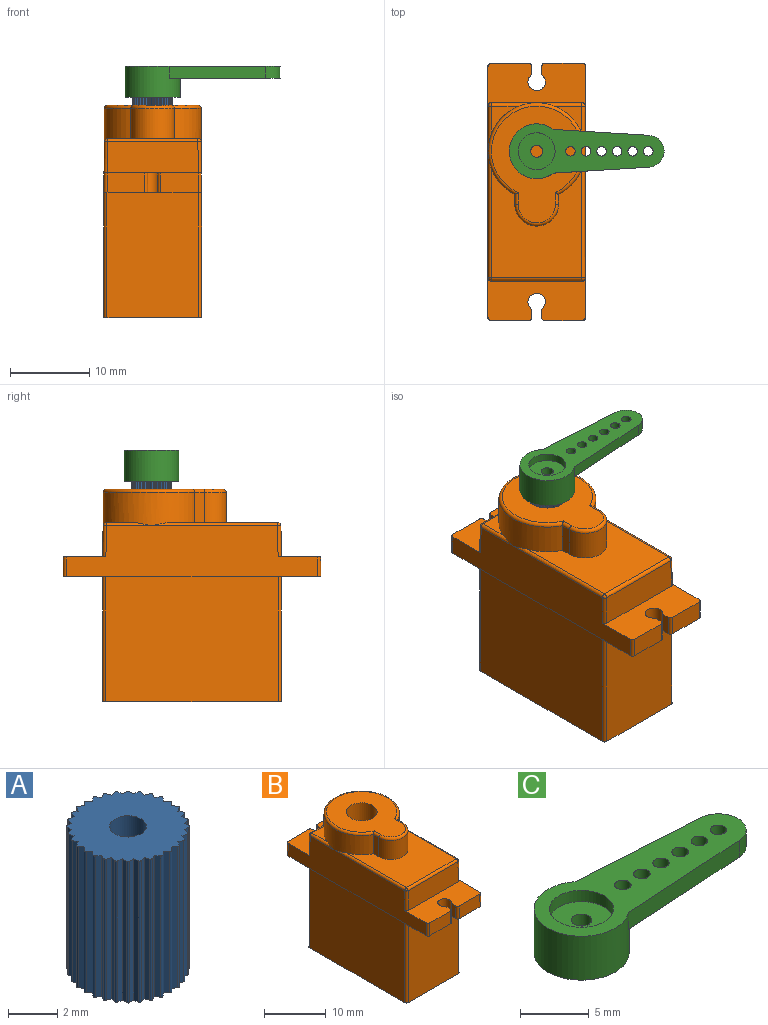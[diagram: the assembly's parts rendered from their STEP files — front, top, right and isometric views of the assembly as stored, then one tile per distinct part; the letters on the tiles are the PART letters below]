
ASSEMBLY  parts=3 mates=2
PART A: 99 faces, bbox 5x5x7.1 mm
  f0: plane 5x5mm, normal (0,0,-1), area 16.5mm2, adj f1,f2,f3,f4,f5,f6,f7,f8
  f1: plane 7.05x0.2mm, normal (-0.8,0.6,0), area 1.7mm2, adj f0,f2,f94,f95
  f2: cylinder r=0.08mm len=7.05mm, axis (0,0,-1), area 0.9mm2, adj f0,f1,f3,f94
  f3: plane 7.05x0.21mm, normal (-0.51,-0.86,0), area 1.7mm2, adj f0,f2,f4,f94
  f4: plane 7.05x0.22mm, normal (-0.9,0.43,0), area 1.7mm2, adj f0,f3,f5,f94
  f5: cylinder r=0.08mm len=7.05mm, axis (0,0,-1), area 0.9mm2, adj f0,f4,f6,f94
  f6: plane 7.05x0.23mm, normal (-0.33,-0.94,0), area 1.7mm2, adj f0,f5,f7,f94
  f7: plane 7.05x0.24mm, normal (-0.97,0.25,0), area 1.7mm2, adj f0,f6,f8,f94
  f8: cylinder r=0.08mm len=7.05mm, axis (0,0,-1), area 0.9mm2, adj f0,f7,f9,f94
  f9: plane 7.05x0.25mm, normal (-0.14,-0.99,0), area 1.7mm2, adj f0,f8,f10,f94
  f10: plane 7.05x0.25mm, normal (-1,0.05,0), area 1.7mm2, adj f0,f9,f11,f94
  f11: cylinder r=0.08mm len=7.05mm, axis (0,0,-1), area 0.9mm2, adj f0,f10,f12,f94
  f12: plane 7.05x0.25mm, normal (0.05,-1,0), area 1.7mm2, adj f0,f11,f13,f94
  f13: plane 7.05x0.25mm, normal (-0.99,-0.14,0), area 1.7mm2, adj f0,f12,f14,f94
  f14: cylinder r=0.08mm len=7.05mm, axis (0,0,-1), area 0.9mm2, adj f0,f13,f15,f94
  f15: plane 7.05x0.24mm, normal (0.25,-0.97,0), area 1.7mm2, adj f0,f14,f16,f94
  f16: plane 7.05x0.23mm, normal (-0.94,-0.33,0), area 1.7mm2, adj f0,f15,f17,f94
  f17: cylinder r=0.08mm len=7.05mm, axis (0,0,-1), area 0.9mm2, adj f0,f16,f18,f94
  f18: plane 7.05x0.22mm, normal (0.43,-0.9,0), area 1.7mm2, adj f0,f17,f19,f94
  f19: plane 7.05x0.21mm, normal (-0.86,-0.51,0), area 1.7mm2, adj f0,f18,f20,f94
  f20: cylinder r=0.08mm len=7.05mm, axis (0,0,-1), area 0.9mm2, adj f0,f19,f21,f94
  f21: plane 7.05x0.2mm, normal (0.6,-0.8,0), area 1.7mm2, adj f0,f20,f22,f94
  f22: plane 7.05x0.18mm, normal (-0.74,-0.67,0), area 1.7mm2, adj f0,f21,f23,f94
  f23: cylinder r=0.08mm len=7.05mm, axis (0,0,-1), area 0.9mm2, adj f0,f22,f24,f94
  f24: plane 7.05x0.18mm, normal (0.74,-0.67,0), area 1.7mm2, adj f0,f23,f25,f94
  f25: plane 7.05x0.2mm, normal (-0.6,-0.8,0), area 1.7mm2, adj f0,f24,f26,f94
  f26: cylinder r=0.08mm len=7.05mm, axis (0,0,-1), area 0.9mm2, adj f0,f25,f27,f94
  f27: plane 7.05x0.21mm, normal (0.86,-0.51,0), area 1.7mm2, adj f0,f26,f28,f94
  f28: plane 7.05x0.22mm, normal (-0.43,-0.9,0), area 1.7mm2, adj f0,f27,f29,f94
  f29: cylinder r=0.08mm len=7.05mm, axis (0,0,-1), area 0.9mm2, adj f0,f28,f30,f94
  f30: plane 7.05x0.23mm, normal (0.94,-0.33,0), area 1.7mm2, adj f0,f29,f31,f94
  f31: plane 7.05x0.24mm, normal (-0.25,-0.97,0), area 1.7mm2, adj f0,f30,f32,f94
  f32: cylinder r=0.08mm len=7.05mm, axis (0,0,-1), area 0.9mm2, adj f0,f31,f33,f94
  f33: plane 7.05x0.25mm, normal (0.99,-0.14,0), area 1.7mm2, adj f0,f32,f34,f94
  f34: plane 7.05x0.25mm, normal (-0.05,-1,0), area 1.7mm2, adj f0,f33,f35,f94
  f35: cylinder r=0.08mm len=7.05mm, axis (0,0,-1), area 0.9mm2, adj f0,f34,f36,f94
  f36: plane 7.05x0.25mm, normal (1,0.05,0), area 1.7mm2, adj f0,f35,f37,f94
  f37: plane 7.05x0.25mm, normal (0.14,-0.99,0), area 1.7mm2, adj f0,f36,f38,f94
  f38: cylinder r=0.08mm len=7.05mm, axis (0,0,-1), area 0.9mm2, adj f0,f37,f39,f94
  f39: plane 7.05x0.24mm, normal (0.97,0.25,0), area 1.7mm2, adj f0,f38,f40,f94
  f40: plane 7.05x0.23mm, normal (0.33,-0.94,0), area 1.7mm2, adj f0,f39,f41,f94
  f41: cylinder r=0.08mm len=7.05mm, axis (0,0,-1), area 0.9mm2, adj f0,f40,f42,f94
  f42: plane 7.05x0.22mm, normal (0.9,0.43,0), area 1.7mm2, adj f0,f41,f43,f94
  f43: plane 7.05x0.21mm, normal (0.51,-0.86,0), area 1.7mm2, adj f0,f42,f44,f94
  f44: cylinder r=0.08mm len=7.05mm, axis (0,0,-1), area 0.9mm2, adj f0,f43,f45,f94
  f45: plane 7.05x0.2mm, normal (0.8,0.6,0), area 1.7mm2, adj f0,f44,f46,f94
  f46: plane 7.05x0.18mm, normal (0.67,-0.74,0), area 1.7mm2, adj f0,f45,f47,f94
  f47: cylinder r=0.08mm len=7.05mm, axis (0,0,-1), area 0.9mm2, adj f0,f46,f48,f94
  f48: plane 7.05x0.18mm, normal (0.67,0.74,0), area 1.7mm2, adj f0,f47,f49,f94
  f49: plane 7.05x0.2mm, normal (0.8,-0.6,0), area 1.7mm2, adj f0,f48,f50,f94
  f50: cylinder r=0.08mm len=7.05mm, axis (0,0,-1), area 0.9mm2, adj f0,f49,f51,f94
  f51: plane 7.05x0.21mm, normal (0.51,0.86,0), area 1.7mm2, adj f0,f50,f52,f94
  f52: plane 7.05x0.22mm, normal (0.9,-0.43,0), area 1.7mm2, adj f0,f51,f53,f94
  f53: cylinder r=0.08mm len=7.05mm, axis (0,0,-1), area 0.9mm2, adj f0,f52,f54,f94
  f54: plane 7.05x0.23mm, normal (0.33,0.94,0), area 1.7mm2, adj f0,f53,f55,f94
  f55: plane 7.05x0.24mm, normal (0.97,-0.25,0), area 1.7mm2, adj f0,f54,f56,f94
  f56: cylinder r=0.08mm len=7.05mm, axis (0,0,-1), area 0.9mm2, adj f0,f55,f57,f94
  f57: plane 7.05x0.25mm, normal (0.14,0.99,0), area 1.7mm2, adj f0,f56,f58,f94
  f58: plane 7.05x0.25mm, normal (1,-0.05,0), area 1.7mm2, adj f0,f57,f59,f94
  f59: cylinder r=0.08mm len=7.05mm, axis (0,0,-1), area 0.9mm2, adj f0,f58,f60,f94
  f60: plane 7.05x0.25mm, normal (-0.05,1,0), area 1.7mm2, adj f0,f59,f61,f94
  f61: plane 7.05x0.25mm, normal (0.99,0.14,0), area 1.7mm2, adj f0,f60,f62,f94
  f62: cylinder r=0.08mm len=7.05mm, axis (0,0,-1), area 0.9mm2, adj f0,f61,f63,f94
  f63: plane 7.05x0.24mm, normal (-0.25,0.97,0), area 1.7mm2, adj f0,f62,f64,f94
  f64: plane 7.05x0.23mm, normal (0.94,0.33,0), area 1.7mm2, adj f0,f63,f65,f94
  f65: cylinder r=0.08mm len=7.05mm, axis (0,0,-1), area 0.9mm2, adj f0,f64,f66,f94
  f66: plane 7.05x0.22mm, normal (-0.43,0.9,0), area 1.7mm2, adj f0,f65,f67,f94
  f67: plane 7.05x0.21mm, normal (0.86,0.51,0), area 1.7mm2, adj f0,f66,f68,f94
  f68: cylinder r=0.08mm len=7.05mm, axis (0,0,-1), area 0.9mm2, adj f0,f67,f69,f94
  f69: plane 7.05x0.2mm, normal (-0.6,0.8,0), area 1.7mm2, adj f0,f68,f70,f94
  f70: plane 7.05x0.18mm, normal (0.74,0.67,0), area 1.7mm2, adj f0,f69,f71,f94
  f71: cylinder r=0.08mm len=7.05mm, axis (0,0,-1), area 0.9mm2, adj f0,f70,f72,f94
  f72: plane 7.05x0.18mm, normal (-0.74,0.67,0), area 1.7mm2, adj f0,f71,f73,f94
  f73: plane 7.05x0.2mm, normal (0.6,0.8,0), area 1.7mm2, adj f0,f72,f74,f94
  f74: cylinder r=0.08mm len=7.05mm, axis (0,0,-1), area 0.9mm2, adj f0,f73,f75,f94
  f75: plane 7.05x0.21mm, normal (-0.86,0.51,0), area 1.7mm2, adj f0,f74,f76,f94
  f76: plane 7.05x0.22mm, normal (0.43,0.9,0), area 1.7mm2, adj f0,f75,f77,f94
  f77: cylinder r=0.08mm len=7.05mm, axis (0,0,-1), area 0.9mm2, adj f0,f76,f78,f94
  f78: plane 7.05x0.23mm, normal (-0.94,0.33,0), area 1.7mm2, adj f0,f77,f79,f94
  f79: plane 7.05x0.24mm, normal (0.25,0.97,0), area 1.7mm2, adj f0,f78,f80,f94
  f80: cylinder r=0.08mm len=7.05mm, axis (0,0,-1), area 0.9mm2, adj f0,f79,f81,f94
  f81: plane 7.05x0.25mm, normal (-0.99,0.14,0), area 1.7mm2, adj f0,f80,f82,f94
  f82: plane 7.05x0.25mm, normal (0.05,1,0), area 1.7mm2, adj f0,f81,f83,f94
  f83: cylinder r=0.08mm len=7.05mm, axis (0,0,-1), area 0.9mm2, adj f0,f82,f84,f94
  f84: plane 7.05x0.25mm, normal (-1,-0.05,0), area 1.7mm2, adj f0,f83,f85,f94
  f85: plane 7.05x0.25mm, normal (-0.14,0.99,0), area 1.7mm2, adj f0,f84,f86,f94
  f86: cylinder r=0.08mm len=7.05mm, axis (0,0,-1), area 0.9mm2, adj f0,f85,f87,f94
  f87: plane 7.05x0.24mm, normal (-0.97,-0.25,0), area 1.7mm2, adj f0,f86,f88,f94
  f88: plane 7.05x0.23mm, normal (-0.33,0.94,0), area 1.7mm2, adj f0,f87,f89,f94
  f89: cylinder r=0.08mm len=7.05mm, axis (0,0,-1), area 0.9mm2, adj f0,f88,f90,f94
  f90: plane 7.05x0.22mm, normal (-0.9,-0.43,0), area 1.7mm2, adj f0,f89,f91,f94
  f91: plane 7.05x0.21mm, normal (-0.51,0.86,0), area 1.7mm2, adj f0,f90,f92,f94
  f92: cylinder r=0.08mm len=7.05mm, axis (0,0,-1), area 0.9mm2, adj f0,f91,f93,f94
  f93: plane 7.05x0.2mm, normal (-0.8,-0.6,0), area 1.7mm2, adj f0,f92,f94,f96
  f94: plane 5x5mm, normal (0,0,1), area 16.5mm2, adj f1,f2,f3,f4,f5,f6,f7,f8
  f95: plane 7.05x0.18mm, normal (-0.67,-0.74,0), area 1.7mm2, adj f0,f1,f94,f97
  f96: plane 7.05x0.18mm, normal (-0.67,0.74,0), area 1.7mm2, adj f0,f93,f94,f97
  f97: cylinder r=0.08mm len=7.05mm, axis (0,0,-1), area 0.9mm2, adj f0,f94,f95,f96
  f98: cylinder r=0.75mm len=7.05mm, axis (0,0,-1), area 33.2mm2, adj f0,f94
PART B: 64 faces, bbox 13.2x32.4x26.7 mm
  f0: plane 3.52x3.52mm, normal (0,0,1), area 4.4mm2, adj f4,f7,f57
  f1: plane 3.52x3.52mm, normal (0,0,1), area 4.4mm2, adj f5,f8,f57
  f2: plane 13.72x11.39mm, normal (0,0,1), area 107.7mm2, adj f3,f6,f47,f53,f54,f57,f58
  f3: cylinder r=0.4mm len=15.89mm, axis (0,1,0), area 9.3mm2, adj f2,f17,f45,f57
  f4: cylinder r=0.4mm len=5.69mm, axis (0,1,0), area 2.9mm2, adj f0,f17,f50,f57
  f5: cylinder r=0.4mm len=5.69mm, axis (0,1,0), area 2.9mm2, adj f1,f15,f51,f57
  f6: cylinder r=0.4mm len=15.89mm, axis (0,1,0), area 9.3mm2, adj f2,f15,f49,f57
  f7: cylinder r=0.4mm len=5.69mm, axis (-1,0,0), area 2.9mm2, adj f0,f16,f50,f57
  f8: cylinder r=0.4mm len=5.69mm, axis (-1,0,0), area 2.9mm2, adj f1,f16,f51,f57
  f9: plane 4.73x2.5mm, normal (0,1,0.01), area 11.8mm2, adj f11,f12,f32,f36
  f10: plane 4.73x2.5mm, normal (0,1,0.01), area 11.8mm2, adj f11,f12,f33,f37
  f11: plane 12.3x5.35mm, normal (0,0,-1), area 55.4mm2, adj f9,f10,f15,f17,f22,f29,f30,f31
  f12: plane 12.26x5.35mm, normal (0,0,1), area 55.2mm2, adj f9,f10,f15,f16,f17,f29,f30,f31
  f13: plane 4.73x2.5mm, normal (0,-1,0.01), area 11.8mm2, adj f14,f25,f34,f38
  f14: plane 12.26x5.35mm, normal (0,0,1), area 55.2mm2, adj f13,f15,f17,f18,f24,f26,f27,f28
  f15: plane 31.6x6.4mm, normal (1,0,0.01), area 163.4mm2, adj f5,f6,f11,f12,f14,f23,f25,f36
  f16: plane 11.46x3.9mm, normal (0,1,0.01), area 44.6mm2, adj f7,f8,f12,f48,f52
  f17: plane 31.6x6.4mm, normal (-1,0,0.01), area 163.4mm2, adj f3,f4,f11,f12,f14,f21,f25,f37
  f18: plane 11.46x3.9mm, normal (0,-1,0.01), area 44.6mm2, adj f14,f44,f46,f47
  f19: plane 22.5x12.3mm, normal (0,0,-1), area 276.6mm2, adj f20,f21,f22,f23,f40,f41,f42,f43
  f20: plane 15.7x11.5mm, normal (0,-1,0), area 180.5mm2, adj f19,f25,f42,f43
  f21: plane 21.7x15.7mm, normal (-1,0,0), area 340.7mm2, adj f17,f19,f41,f42
  f22: plane 15.7x11.5mm, normal (0,1,0), area 180.5mm2, adj f11,f19,f40,f41
  f23: plane 21.7x15.7mm, normal (1,0,0), area 340.7mm2, adj f15,f19,f40,f43
  f24: plane 4.73x2.5mm, normal (0,-1,0.01), area 11.8mm2, adj f14,f25,f35,f39
  f25: plane 12.3x5.35mm, normal (0,0,-1), area 55.4mm2, adj f13,f15,f17,f20,f24,f26,f27,f28
  f26: cylinder r=1.1mm len=2.5mm, axis (0,0,1), area 14mm2, adj f14,f25,f27,f28
  f27: plane 2.5x1.04mm, normal (1,0,0), area 2.6mm2, adj f14,f25,f26,f34
  f28: plane 2.5x1.04mm, normal (-1,0,0), area 2.6mm2, adj f14,f25,f26,f35
  f29: plane 2.5x1.04mm, normal (-1,0,0), area 2.6mm2, adj f11,f12,f31,f32
  f30: plane 2.5x1.04mm, normal (1,0,0), area 2.6mm2, adj f11,f12,f31,f33
  f31: cylinder r=1.1mm len=2.5mm, axis (0,0,1), area 14mm2, adj f11,f12,f29,f30
  f32: cylinder r=0.4mm len=2.51mm, axis (0,0.01,-1), area 1.6mm2, adj f9,f11,f12,f29
  f33: cylinder r=0.4mm len=2.51mm, axis (0,-0.01,1), area 1.6mm2, adj f10,f11,f12,f30
  f34: cylinder r=0.4mm len=2.51mm, axis (0,0.01,1), area 1.6mm2, adj f13,f14,f25,f27
  f35: cylinder r=0.4mm len=2.51mm, axis (0,-0.01,-1), area 1.6mm2, adj f14,f24,f25,f28
  f36: cylinder r=0.4mm len=2.5mm, axis (0.01,0.01,-1), area 1.6mm2, adj f9,f11,f12,f15
  f37: cylinder r=0.4mm len=2.5mm, axis (-0.01,0.01,-1), area 1.6mm2, adj f10,f11,f12,f17
  f38: cylinder r=0.4mm len=2.5mm, axis (-0.01,-0.01,-1), area 1.6mm2, adj f13,f14,f17,f25
  f39: cylinder r=0.4mm len=2.5mm, axis (0.01,-0.01,-1), area 1.6mm2, adj f14,f15,f24,f25
  f40: cylinder r=0.4mm len=15.7mm, axis (0,0,-1), area 9.9mm2, adj f11,f19,f22,f23
  f41: cylinder r=0.4mm len=15.7mm, axis (0,0,1), area 9.9mm2, adj f11,f19,f21,f22
  f42: cylinder r=0.4mm len=15.7mm, axis (0,0,-1), area 9.9mm2, adj f19,f20,f21,f25
  f43: cylinder r=0.4mm len=15.7mm, axis (0,0,1), area 9.9mm2, adj f19,f20,f23,f25
  f44: cylinder r=0.4mm len=3.91mm, axis (-0.01,-0.01,-1), area 2.5mm2, adj f14,f17,f18,f45
  f45: sphere r=0.4mm, area 0.2mm2, adj f3,f44,f47
  f46: cylinder r=0.4mm len=3.91mm, axis (0.01,-0.01,-1), area 2.5mm2, adj f14,f15,f18,f49
  f47: cylinder r=0.4mm len=11.39mm, axis (-1,0,0), area 7.1mm2, adj f2,f18,f45,f49
  f48: cylinder r=0.4mm len=3.91mm, axis (-0.01,0.01,-1), area 2.5mm2, adj f12,f16,f17,f50
  f49: sphere r=0.4mm, area 0.2mm2, adj f6,f46,f47
  f50: sphere r=0.4mm, area 0.2mm2, adj f4,f7,f48
  f51: sphere r=0.4mm, area 0.2mm2, adj f5,f8,f52
  f52: cylinder r=0.4mm len=3.91mm, axis (0.01,0.01,-1), area 2.5mm2, adj f12,f15,f16,f51
  f53: plane 3.8x1.22mm, normal (-1,0,0), area 4.6mm2, adj f2,f54,f57,f61
  f54: cylinder r=2.75mm len=5.5mm, axis (0,0,-1), area 32.8mm2, adj f2,f53,f58,f63
  f55: plane 14.7x11.39mm, normal (0,0,1), area 96.2mm2, adj f56,f60,f61,f62,f63
  f56: cylinder r=2.5mm len=5mm, axis (0,0,-1), area 66mm2, adj f55,f59
  f57: cylinder r=6.09mm len=12.19mm, axis (0,0,-1), area 125.9mm2, adj f0,f1,f2,f3,f4,f5,f6,f7
  f58: plane 3.8x1.22mm, normal (1,0,0), area 4.6mm2, adj f2,f54,f57,f62
  f59: plane 5x5mm, normal (0,0,1), area 19.6mm2, adj f56
  f60: torus R=5.69mm, axis (0,0,1), area 20.1mm2, adj f55,f57,f61,f62
  f61: cylinder r=0.4mm len=1.47mm, axis (0,1,0), area 0.8mm2, adj f53,f55,f60,f63
  f62: cylinder r=0.4mm len=1.47mm, axis (0,-1,0), area 0.8mm2, adj f55,f58,f60,f63
  f63: torus R=2.35mm, axis (0,0,1), area 5.1mm2, adj f54,f55,f61,f62
PART C: 18 faces, bbox 19.5x6.9x3.9 mm
  f0: plane 4.65x4.65mm, normal (0,0,1), area 15.2mm2, adj f1,f7
  f1: cylinder r=0.75mm len=1.5mm, axis (0,0,-1), area 4.9mm2, adj f0,f2
  f2: plane 5x5mm, normal (0,0,-1), area 17.9mm2, adj f1,f3
  f3: cylinder r=2.5mm len=5mm, axis (0,0,-1), area 29.1mm2, adj f2,f4
  f4: plane 6.9x6.9mm, normal (0,0,-1), area 17.8mm2, adj f3,f5
  f5: cylinder r=3.45mm len=6.9mm, axis (0,0,-1), area 75mm2, adj f4,f6,f8,f9,f11
  f6: plane 19.5x6.9mm, normal (0,0,1), area 71.6mm2, adj f5,f7,f8,f9,f10,f12,f13,f14
  f7: cylinder r=2.32mm len=4.65mm, axis (0,0,-1), area 14.6mm2, adj f0,f6
  f8: plane 12.09x1.5mm, normal (0.06,1,0), area 18.2mm2, adj f5,f6,f10,f11
  f9: plane 12.09x1.5mm, normal (0.06,-1,0), area 18.2mm2, adj f5,f6,f10,f11
  f10: cylinder r=2mm len=4mm, axis (0,0,1), area 9.1mm2, adj f6,f8,f9,f11
  f11: plane 13.97x5.5mm, normal (0,0,-1), area 51.2mm2, adj f5,f8,f9,f10,f12,f13,f14,f15
  f12: cylinder r=0.6mm len=1.5mm, axis (0,0,1), area 5.7mm2, adj f6,f11
  f13: cylinder r=0.6mm len=1.5mm, axis (0,0,1), area 5.7mm2, adj f6,f11
  f14: cylinder r=0.6mm len=1.5mm, axis (0,0,1), area 5.7mm2, adj f6,f11
  f15: cylinder r=0.6mm len=1.5mm, axis (0,0,1), area 5.7mm2, adj f6,f11
  f16: cylinder r=0.6mm len=1.5mm, axis (0,0,1), area 5.7mm2, adj f6,f11
  f17: cylinder r=0.6mm len=1.5mm, axis (0,0,1), area 5.7mm2, adj f6,f11
PLACE A rot(axis=(0,0,1),90deg) t=(5.1,5.1,0)mm
PLACE B at identity fixed
PLACE C at identity
MATE revolute B.f56 <-> A.f98  axis (0,0,-1) through (0,5.1,6.8)mm
MATE fastened A.f98 <-> C.f1  axis (0,0,1) through (0,5.1,13.85)mm
